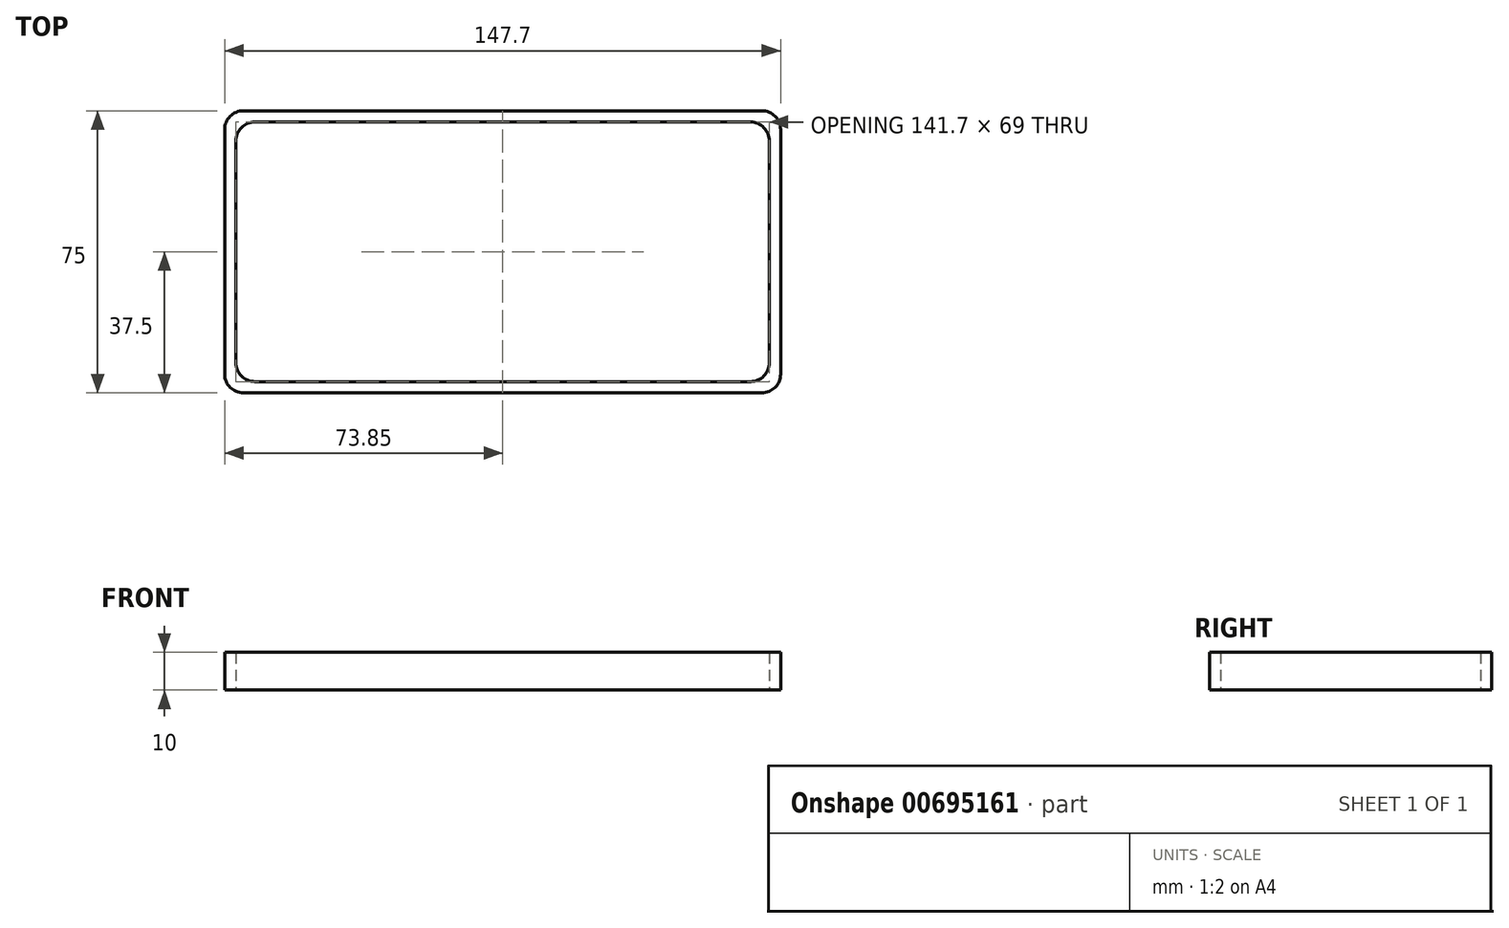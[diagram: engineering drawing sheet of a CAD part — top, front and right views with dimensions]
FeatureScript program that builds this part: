
annotation { "Feature Type Name" : "Feature", "Feature Type Description" : "" }
export const myFeature = defineFeature(function(context is Context, id is Id, definition is map)
    precondition{}
    {
        {
            var Q0;
            Q0=qCreatedBy(makeId("Top.planeOp"),FACE);
            var sketch = newSketch(context, id + "F0", { "sketchPlane" : qUnion([Q0])});
            skLineSegment(sketch, "E0.bottom", {"start": v(65.85, -34.5) * mm, "end": v(-65.85, -34.5) * mm});
            skLineSegment(sketch, "E0.top", {"start": v(65.85, 34.5) * mm, "end": v(-65.85, 34.5) * mm});
            skLineSegment(sketch, "E0.left", {"start": v(70.85, -29.5) * mm, "end": v(70.85, 29.5) * mm});
            skLineSegment(sketch, "E0.right", {"start": v(-70.85, -29.5) * mm, "end": v(-70.85, 29.5) * mm});
            skPoint(sketch, "E0.middle", {"position": v(0, 0) * mm});
            skPoint(sketch, "E1.visualSharp", {"position": v(-70.85, -34.5) * mm});
            skArc(sketch, "E1.filletArc", {"start": v(-70.85, -29.5) * mm, "mid": v(-69.39, -33.04) * mm, "end": v(-65.85, -34.5) * mm});
            skPoint(sketch, "E2.visualSharp", {"position": v(-70.85, 34.5) * mm});
            skArc(sketch, "E2.filletArc", {"start": v(-65.85, 34.5) * mm, "mid": v(-69.39, 33.04) * mm, "end": v(-70.85, 29.5) * mm});
            skPoint(sketch, "E3.visualSharp", {"position": v(70.85, 34.5) * mm});
            skArc(sketch, "E3.filletArc", {"start": v(70.85, 29.5) * mm, "mid": v(69.39, 33.04) * mm, "end": v(65.85, 34.5) * mm});
            skPoint(sketch, "E4.visualSharp", {"position": v(70.85, -34.5) * mm});
            skArc(sketch, "E4.filletArc", {"start": v(65.85, -34.5) * mm, "mid": v(69.39, -33.04) * mm, "end": v(70.85, -29.5) * mm});
            skLineSegment(sketch, "E5.bottom", {"start": v(68.85, -37.5) * mm, "end": v(-68.85, -37.5) * mm});
            skLineSegment(sketch, "E5.top", {"start": v(68.85, 37.5) * mm, "end": v(-68.85, 37.5) * mm});
            skLineSegment(sketch, "E5.left", {"start": v(73.85, -32.5) * mm, "end": v(73.85, 32.5) * mm});
            skLineSegment(sketch, "E5.right", {"start": v(-73.85, -32.5) * mm, "end": v(-73.85, 32.5) * mm});
            skPoint(sketch, "E6.visualSharp", {"position": v(-73.85, 37.5) * mm});
            skArc(sketch, "E6.filletArc", {"start": v(-68.85, 37.5) * mm, "mid": v(-72.39, 36.04) * mm, "end": v(-73.85, 32.5) * mm});
            skPoint(sketch, "E7.visualSharp", {"position": v(73.85, 37.5) * mm});
            skArc(sketch, "E7.filletArc", {"start": v(73.85, 32.5) * mm, "mid": v(72.39, 36.04) * mm, "end": v(68.85, 37.5) * mm});
            skPoint(sketch, "E8.visualSharp", {"position": v(73.85, -37.5) * mm});
            skArc(sketch, "E8.filletArc", {"start": v(68.85, -37.5) * mm, "mid": v(72.39, -36.04) * mm, "end": v(73.85, -32.5) * mm});
            skPoint(sketch, "E9.visualSharp", {"position": v(-73.85, -37.5) * mm});
            skArc(sketch, "E9.filletArc", {"start": v(-73.85, -32.5) * mm, "mid": v(-72.39, -36.04) * mm, "end": v(-68.85, -37.5) * mm});
            skSolve(sketch);
        }
        {
            var Q0;
            Q0 = qSketchRegion(id + "F0", true);
            extrude(context, id + "F1", {"entities" : qUnion([Q0]), "depth" : 10 * mm, "offsetDistance" : 25 * mm});
        }
    });
